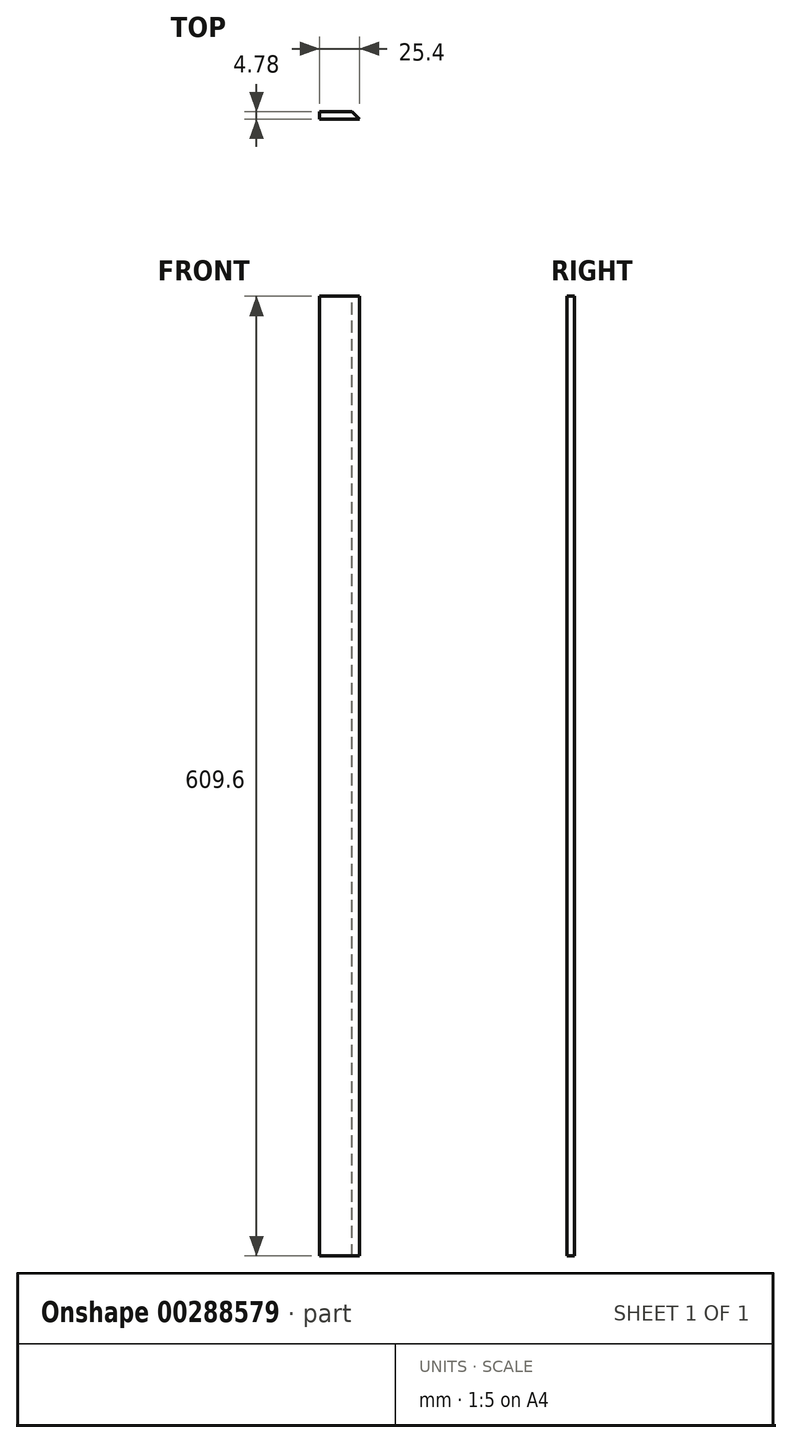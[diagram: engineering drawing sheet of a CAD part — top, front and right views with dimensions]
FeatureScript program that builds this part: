
annotation { "Feature Type Name" : "Feature", "Feature Type Description" : "" }
export const myFeature = defineFeature(function(context is Context, id is Id, definition is map)
    precondition{}
    {
        {
            var Q0;
            Q0=qCreatedBy(makeId("Front.planeOp"),FACE);
            var sketch = newSketch(context, id + "F0", { "sketchPlane" : qUnion([Q0])});
            skLineSegment(sketch, "E0.bottom", {"start": v(12.7, 304.8) * mm, "end": v(-12.7, 304.8) * mm});
            skLineSegment(sketch, "E0.top", {"start": v(12.7, -304.8) * mm, "end": v(-12.7, -304.8) * mm});
            skLineSegment(sketch, "E0.left", {"start": v(12.7, 304.8) * mm, "end": v(12.7, -304.8) * mm});
            skLineSegment(sketch, "E0.right", {"start": v(-12.7, 304.8) * mm, "end": v(-12.7, -304.8) * mm});
            skPoint(sketch, "E0.middle", {"position": v(0, 0) * mm});
            skSolve(sketch);
        }
        {
            var Q0;
            Q0=qSketchRegion(id+"F0",true);
            extrude(context, id + "F1", {"entities" : qUnion([Q0]), "depth" : 4.78 * mm});
        }
        {
            var Q0;
            Q0=makeQuery(id+"F1.opExtrude","SWEPT_FACE",FACE,{"disambiguationData":[OSD([sQuery(id+"F0.wireOp",EDGE,"E0.bottom")])]});
            var sketch = newSketch(context, id + "F2", { "sketchPlane" : qUnion([Q0])});
            skLineSegment(sketch, "E1", {"start": v(12.7, -4.78) * mm, "end": v(7.92, 0) * mm});
            skLineSegment(sketch, "E2", {"start": v(7.92, 0) * mm, "end": v(12.7, 0) * mm});
            skLineSegment(sketch, "E3", {"start": v(12.7, 0) * mm, "end": v(12.7, -4.78) * mm});
            skSolve(sketch);
        }
        {
            var Q0;
            Q0=makeQuery(id+"F2.imprint","IMPRINT",FACE,{"disambiguationData":[TD([[makeQuery(id+"F2.imprint","IMPRINT",EDGE,{"derivedFrom":sQuery(id+"F2.wireOp",EDGE,"E1")}),-1.0]])]});
            extrude(context, id + "F3", {"entities" : qUnion([Q0]), "operationType" : NewBodyOperationType.REMOVE, "endBound" : BoundingType.THROUGH_ALL, "oppositeDirection" : true, "depth" : 25.4 * mm});
        }
    });
